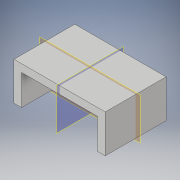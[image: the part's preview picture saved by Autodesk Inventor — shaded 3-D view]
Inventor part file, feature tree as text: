
AUTODESK INVENTOR PART (.ipt)
format: ipt  version: 2017 (Build 210142000, 142)  size: 117,248 bytes
history: native  units: in
note: dims shown in document units (in); Inventor stores cm internally (conversion verified against a paired STEP export)
features: sketch x3, extrude x2, plane x2
ambient origin geometry x8: Origin, YZ Plane, XZ Plane, XY Plane, X Axis, Y Axis, Z Axis, Center Point
bodies: Solid1 (feature_tree)
feature tree (7):
  extrude  "Extrusion1"  Depth=0.25in
  sketch  "Sketch2"  dims[d2=0.25in d3=2.5in]
  plane  "Work Plane1"
  plane  "Work Plane2"
  extrude  "Extrusion2"  Depth=2.5in
  sketch  "Sketch1"  dims[d0=0.25in d1=0.25in]
  sketch  "Sketch3"  dims[d4=1.25in d5=2.0in d6=0.0in d7=0.13in d8=0.25in d9=0.125in d10=0.5in d11=0.0in]
